FCSTD DOCUMENT  (FreeCAD 1.1R40077 (Git))
Label: Variables
License: All rights reserved
LicenseURL: https://en.wikipedia.org/wiki/All_rights_reserved
objects: Spreadsheet::Sheet×1

FEATURE [Spreadsheet::Sheet] Spreadsheet  label="Variables"
  cells = A1='M4 Through OD; B1='M3 Through OD; C1='M4 Tap Diameter; D1='Washer grab diameter; A2(M4ThroughBoreDiam)=4.35; B2(M3ThroughBoreDiam)=3.5; C2(M4TapDiam)=3.6; D2(WasherGrabDiam)=30.5; A5='Wheel Base Size; B5='Slides Mount Offset; C5='Claw Height; D5='Passive Claw Mount X; E5='Passive Claw Mount Y; F5='Wheel ClampToShaft Dist; G5='Wheel Diam; H5='Support Slider Mount Line Dist; I5='Slider Pole Diam; J5='Slider Tolerance; K5='Passive Claw Mount Offset; L5='Clamp Z Offset; M5='SlidesMountX; N5='SlidesMountY; A6(WheelBaseSize)=100; B6(SlidesMountOffset)=55; C6(ClawHeight)==1.6 * 5 + 3; D6(PassiveClawMountX)=12; E6(PassiveClawMountY)=6; F6(WheelClampToShaftDist)=1.5; G6(WheelDiam)==55 mm; H6(SupportSliderMountLineDist)=20; I6(SliderPoleDiam)=10; J6(SliderTolerance)==0 mm; K6(PassiveClawMountOffset)=25; L6(ClampZOffset)=1; M6(SlidesMountX)=45; N6(SlidesMountY)=20; A8='Spool Thickness; B8='Spool Wall Thickness; C8='Spool Inner Diam; A9(SpoolThickness)=35; B9(SpoolWallThickness)=5; C9(SpoolInnerDiam)=15
